# Revit family: WCPan-WallMounted-54cm-Vitra-S50Series_5618L003-0850
name_source: partatom
category: Plumbing Fixtures
revit_build: Autodesk Revit 2017 (Build: 20160225_1515(x64)
units: mm (PartAtom-declared; Revit-internal decimal feet)

## family parameters
Cut with Voids When Loaded = No
Host = Face
OmniClass Number = 23.45.05.21.11
OmniClass Title = Water Closets
Part Type = Normal
Room Calculation Point = No
Round Connector Dimension = Use Diameter
Shared = Yes

## types (4) — shared parameters
BIMobject category = Sanitary - Toilets
CW Connection = Yes
Color = White
Default Elevation = 400 mm  [stored 1.31234 ft]
Design country = Turkey
HW Connection = No
IFC Classification = Sanitary Terminal
Main Material = Ceramic
Manufacturer = Vitra
Manufacturer name = Vitra
Masterformat 2014 Code = 22 45 26
Masterformat 2014 Description = Sanitary Facilities
MountingType = Wall Mounted
NBS Referans Code = 35-65-90
NBS Referans Description = Toilet Systems
Nominal Depth (mm) = 545 mm  [stored 1.78806 ft]
Nominal Height (mm) = 350 mm
Nominal Width (mm) = 365 mm  [stored 1.19751 ft]
OmniClass Code = 23-31 19 00
OmniClass Description = Toilets
Product certification = https://vitraglobal.com
Product family = S50
Product group = Wall Mounted WC
Secondary Material = Ceramic-White
UNSPSC Code = 301815
UNSPSC Description = Sanitary Ware
URL = https://www.vitra.com.tr
Uniclass 1.4 Code = L7216
Uniclass 1.4 Description = Toilets
Uniclass 2.0 Code = SS-35-65-90
Uniclass 2.0 Description = Toilet Systems
Uniclass 2015 Code = Pr_40_20_93
Uniclass 2015 Name = Urinal and WC fittings
Uniformat II Code = D2010
Uniformat II Description = Sanitary Facilities
Vent Connection = No
Warranty Period (Year) = 10 Years
Waste Connection = Yes
Weight Net (kg) = 29,140
Youtube = https://www.youtube.com
zero-valued in all types: Cost

## per-type parameters (varying)
| type | Article No. (default) | Description | Model | Product SKU | Without Pipe |
| WCPan-WallMounted-54cm-Vitra-S50Series_5618L003-0850 | 5618L003-0850 | VitrA  WCPan - Wall Mounted - 54cm - S50 Series | 5618L003-0850 | 5618L003-0850 | Yes |
| WCPan-WallMounted-54cm-Vitra-S50Series_5618L003-0075 | 5618L003-0850 | VitrA | 5618L003-0850 | 5618L003-0850 | No |
| WCPan-WallMounted-54cm-Vitra-S50Series_5618B003-6037 | 5618B003-6037 | VitrA | 5618B003-6037 | 5618B003-6037 | No |
| WCPan-WallMounted-54cm-Vitra-S50Series_5618B003-6039 | 5618B003-6039 | VitrA | 5618B003-6039 | 5618B003-6039 | No |

note: [stored X ft] marks values corroborated as IEEE doubles in the binary element streams (Revit-internal decimal feet)

## geometry (parser evidence)
native form markers: Sweep x3
no freeform markers — native parametric forms only
